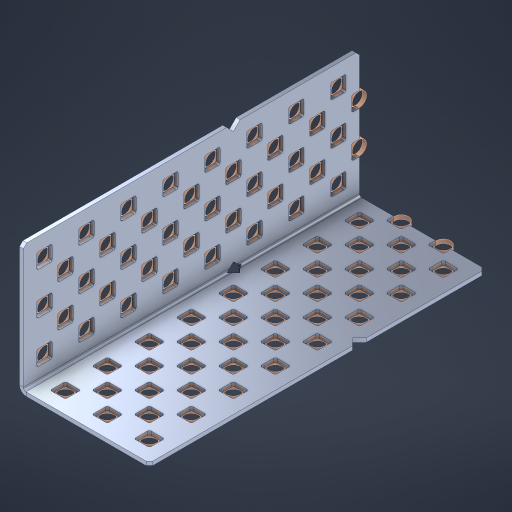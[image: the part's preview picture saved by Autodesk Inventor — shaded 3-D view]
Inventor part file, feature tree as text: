
AUTODESK INVENTOR PART (.ipt)
format: ipt  version: 2023 (Build 270158000, 158)  size: 1,136,128 bytes
history: native  units: in
note: dims shown in document units (in); Inventor stores cm internally (conversion verified against a paired STEP export)
features: other x86, extrude x78, sheet_metal_op x8, sketch x7, pattern_linear x3, mirror x1, chamfer x1
ambient origin geometry x8: Origin, YZ Plane, XZ Plane, XY Plane, X Axis, Y Axis, Z Axis, Center Point
bodies: Solid1 (feature_tree), Body (feature_tree)
feature tree (184):
  sheet_metal_op  "Flanges"
  sheet_metal_op  "Body Pattern"
  pattern_linear  "Center Double"  Spacing1=1.5in  [1 undecoded]
  pattern_linear  "Center Pattern"  Spacing1=0.1875in  [1 undecoded]
  other  "Arc Length"
  pattern_linear  "Notch Pattern"  Spacing1=0.0469in  [1 undecoded]
  other  "Diagonal Plane"
  mirror  "Everything Mirrored"
  chamfer  "End Chamfer"
  sketch  "Sketch1"  dims[d0=1.5in]
  other  "Plate1"
  sketch  "Sketch2"  dims[d1=4.0in]
  other  "Plate2"
  sheet_metal_op  "Bend1"
  sheet_metal_op  "Corner1"
  sketch  "Sketch8"  dims[d2=0.0469in]
  sketch  "Sketch9"  dims[d3=0.0469in]
  other  "Srf91"
  sheet_metal_op  "Body Pattern Sketch"
  other  "Srf92"
  sketch  "Sketch13"  dims[d4=0.0234in]
  sketch  "Sketch15"  dims[d5=0.0938in]
  sketch  "Sketch16"  dims[d6=0.0469in d7=1.5in d8=90.0deg d9=0.0312in d10=0.1875in d11=0.0469in d12=0.0469in d49=0.182in d50=0.02in d52=0.25in d53=0.0469in d54=0.0in d55=0.172in d56=1.0in d57=0.0in d85=0.1473in d86=0.1659in d89=0.0469in d90=0.0in d91=0.04in d92=0.0491in d95=2.5in d96=0.04in d97=0.25in d98=45.0deg d106=0.182in d107=0.02in d110=0.0469in d111=0.0in d112=0.172in d113=0.5in d114=0.0in d117=0.5in d126=0.0491in d127=0.1227in d128=0.08in d129=0.04in d130=2.5in d131=0.25in d132=3.1496in d134=0.5in d135=1.1811in d137=0.5in d140=0.5in d141=1.0in d142=0.3937in d144=0.5in d145=0.071in d146=0.7874in d148=0.5in]
  other  "Srf786"
  other  "Srf856"
  other  "Srf889"
  other  "Srf890"
  other  "Srf891"
  other  "Srf1275"
  other  "Srf1276"
  other  "Srf1278"
  other  "Srf1277"
  other  "Srf1285"
  other  "Srf1286"
  other  "Srf1287"
  other  "Srf1445"
  other  "Srf1446"
  other  "Srf1447"
  other  "Srf1448"
  other  "Srf1537"
  other  "Srf1538"
  other  "Srf1539"
  other  "Srf1540"
  other  "Srf2009"
  other  "Srf2010"
  other  "Srf2011"
  other  "Srf2012"
  other  "Srf2013"
  other  "Srf2014"
  other  "Srf2015"
  other  "Srf2016"
  other  "Srf2043"
  other  "Srf2044"
  other  "Srf2045"
  other  "Srf2046"
  other  "Srf2047"
  other  "Srf2048"
  other  "Srf2049"
  other  "Srf2076"
  other  "Srf2077"
  other  "Srf2078"
  other  "Srf2079"
  other  "Srf2080"
  other  "Srf2081"
  other  "Srf2082"
  other  "Srf2083"
  other  "Srf2084"
  other  "Srf2085"
  other  "Srf2086"
  other  "Srf2087"
  other  "Srf2088"
  other  "Srf2089"
  other  "Srf2090"
  other  "Srf2091"
  other  "Srf2092"
  other  "Srf2093"
  other  "Srf2094"
  other  "Srf2095"
  other  "Srf2096"
  other  "Srf2097"
  other  "Srf2179"
  other  "Srf2180"
  other  "Srf2181"
  other  "Srf2182"
  other  "Srf2183"
  other  "Srf2184"
  other  "Srf2185"
  other  "Srf2186"
  other  "Srf2187"
  other  "Srf2188"
  other  "Srf2189"
  other  "Srf2190"
  other  "Srf2191"
  other  "Srf2192"
  other  "Srf2193"
  other  "Srf2194"
  other  "Srf2195"
  other  "Srf2196"
  other  "Srf2197"
  other  "Srf2198"
  other  "Srf2199"
  sheet_metal_op  "Body Stamp"
  sheet_metal_op  "Body Circle"
  other  "Center Stamp"
  other  "Center Circle"
  sheet_metal_op  "Notch"
  extrude  "ExtrusionSrf92"  Depth=0.0469in
  extrude  "ExtrusionSrf856"  Depth=0.182in
  extrude  "ExtrusionSrf889"  Depth=0.02in
  extrude  "ExtrusionSrf890"  Depth=0.25in
  extrude  "ExtrusionSrf891"  Depth=0.0469in
  extrude  "ExtrusionSrf1275"  TaperAngle=0.0deg  [1 undecoded]
  extrude  "ExtrusionSrf1276"  Depth=0.5in
  extrude  "ExtrusionSrf1277"  Depth=0.5in TaperAngle=0.0deg
  extrude  "ExtrusionSrf1345"  Depth=0.5in
  extrude  "ExtrusionSrf1346"  Depth=0.5in
  extrude  "ExtrusionSrf1347"  Depth=0.0469in
  extrude  "ExtrusionSrf1348"  Depth=0.5in TaperAngle=0.0deg
  extrude  "ExtrusionSrf1445"  Depth=0.5in
  extrude  "ExtrusionSrf1446"  Depth=0.25in TaperAngle=45.0deg
  extrude  "ExtrusionSrf1447"  Depth=0.182in
  extrude  "ExtrusionSrf1448"  Depth=0.02in
  extrude  "ExtrusionSrf1537"  Depth=0.0469in
  extrude  "ExtrusionSrf1538"  TaperAngle=0.0deg  [1 undecoded]
  extrude  "ExtrusionSrf1539"  Depth=0.5in
  extrude  "ExtrusionSrf1540"  Depth=0.5in TaperAngle=0.0deg
  extrude  "ExtrusionSrf2009"  Depth=0.5in
  extrude  "ExtrusionSrf2010"  Depth=0.5in
  extrude  "ExtrusionSrf2011"  Depth=0.5in
  extrude  "ExtrusionSrf2012"  Depth=0.5in
  extrude  "ExtrusionSrf2013"  Depth=0.5in
  extrude  "ExtrusionSrf2014"  Depth=0.5in
  extrude  "ExtrusionSrf2015"  Depth=0.25in
  extrude  "ExtrusionSrf2016"  Depth=0.5in
  extrude  "ExtrusionSrf2043"  Depth=0.5in
  extrude  "ExtrusionSrf2044"  Depth=0.5in
  extrude  "ExtrusionSrf2045"  Depth=0.5in
  extrude  "ExtrusionSrf2046"  Depth=0.3937in
  extrude  "ExtrusionSrf2047"  Depth=0.5in
  extrude  "ExtrusionSrf2048"  Depth=0.5in
  extrude  "ExtrusionSrf2049"  [1 undecoded]
  extrude  "ExtrusionSrf2076"  [1 undecoded]
  extrude  "ExtrusionSrf2077"  [1 undecoded]
  extrude  "ExtrusionSrf2078"  [1 undecoded]
  extrude  "ExtrusionSrf2079"  [1 undecoded]
  extrude  "ExtrusionSrf2080"  [1 undecoded]
  extrude  "ExtrusionSrf2081"  [1 undecoded]
  extrude  "ExtrusionSrf2082"  [1 undecoded]
  extrude  "ExtrusionSrf2083"  [1 undecoded]
  extrude  "ExtrusionSrf2084"  [1 undecoded]
  extrude  "ExtrusionSrf2085"  [1 undecoded]
  extrude  "ExtrusionSrf2086"  [1 undecoded]
  extrude  "ExtrusionSrf2087"  [1 undecoded]
  extrude  "ExtrusionSrf2088"  [1 undecoded]
  extrude  "ExtrusionSrf2089"  [1 undecoded]
  extrude  "ExtrusionSrf2090"  [1 undecoded]
  extrude  "ExtrusionSrf2091"  [1 undecoded]
  extrude  "ExtrusionSrf2092"  [1 undecoded]
  extrude  "ExtrusionSrf2093"  [1 undecoded]
  extrude  "ExtrusionSrf2094"  [1 undecoded]
  extrude  "ExtrusionSrf2095"  [1 undecoded]
  extrude  "ExtrusionSrf2096"  [1 undecoded]
  extrude  "ExtrusionSrf2097"  [1 undecoded]
  extrude  "ExtrusionSrf2179"  [1 undecoded]
  extrude  "ExtrusionSrf2180"  [1 undecoded]
  extrude  "ExtrusionSrf2181"  [1 undecoded]
  extrude  "ExtrusionSrf2182"  [1 undecoded]
  extrude  "ExtrusionSrf2183"  [1 undecoded]
  extrude  "ExtrusionSrf2184"  [1 undecoded]
  extrude  "ExtrusionSrf2185"  [1 undecoded]
  extrude  "ExtrusionSrf2186"  [1 undecoded]
  extrude  "ExtrusionSrf2187"  [1 undecoded]
  extrude  "ExtrusionSrf2188"  [1 undecoded]
  extrude  "ExtrusionSrf2189"  [1 undecoded]
  extrude  "ExtrusionSrf2190"  [1 undecoded]
  extrude  "ExtrusionSrf2191"  [1 undecoded]
  extrude  "ExtrusionSrf2192"  [1 undecoded]
  extrude  "ExtrusionSrf2193"  [1 undecoded]
  extrude  "ExtrusionSrf2194"  [1 undecoded]
  extrude  "ExtrusionSrf2195"  [1 undecoded]
  extrude  "ExtrusionSrf2196"  [1 undecoded]
  extrude  "ExtrusionSrf2197"  [1 undecoded]
  extrude  "ExtrusionSrf2198"  [1 undecoded]
  extrude  "ExtrusionSrf2199"  [1 undecoded]
note: 49 required parameter values undecoded (feature->parameter linkage not recoverable at this tier; creation-order binding heuristic only, values carry confidence <= 0.55)
